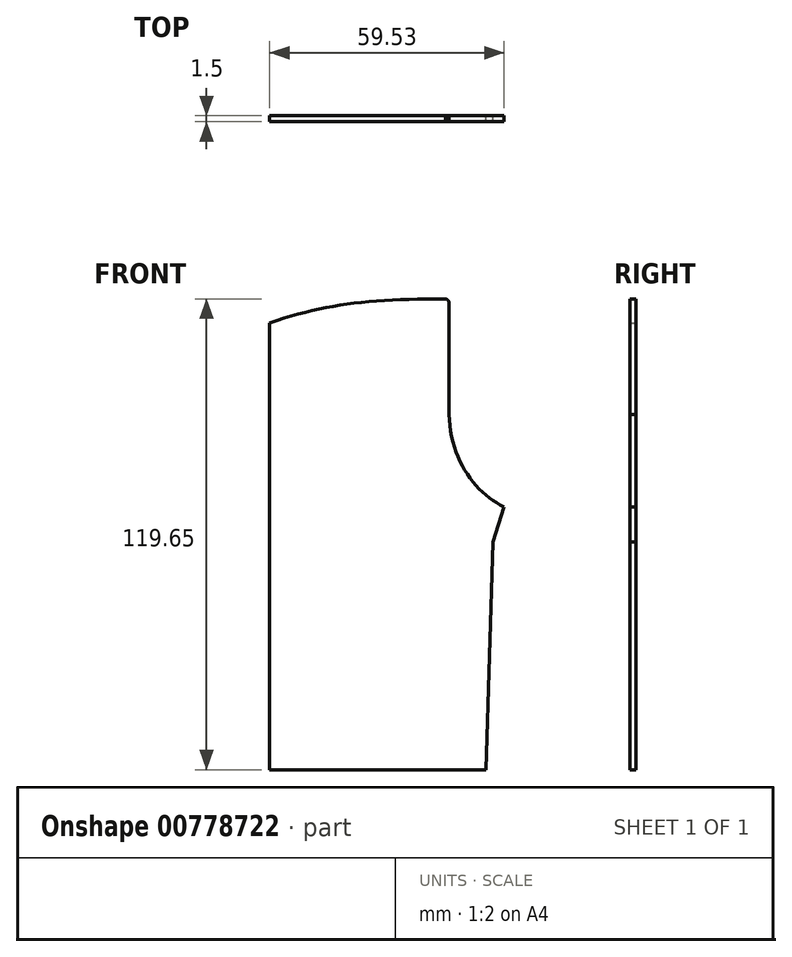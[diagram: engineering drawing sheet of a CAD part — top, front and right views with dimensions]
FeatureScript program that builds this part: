
annotation { "Feature Type Name" : "Feature", "Feature Type Description" : "" }
export const myFeature = defineFeature(function(context is Context, id is Id, definition is map)
    precondition{}
    {
        {
            var Q0;
            Q0=qCreatedBy(makeId("Front.planeOp"),FACE);
            var sketch = newSketch(context, id + "F0", { "sketchPlane" : qUnion([Q0])});
            skLineSegment(sketch, "E0", {"start": v(0, 0) * mm, "end": v(55, 0) * mm});
            skLineSegment(sketch, "E1", {"start": v(55, 0) * mm, "end": v(56.79, 57.84) * mm});
            skLineSegment(sketch, "E2", {"start": v(56.79, 57.84) * mm, "end": v(59.53, 66.82) * mm});
            skLineSegment(sketch, "E3", {"start": v(0, 0) * mm, "end": v(0, 113.54) * mm});
            skFitSpline(sketch, "E4", {"points": [v(0, 113.54) * mm, v(44.65, 119.65) * mm], "startDerivative": vector(42.5, 14.54) * mm, "endDerivative": vector(56.66, 0) * mm});
            skFitSpline(sketch, "E5", {"points": [v(44.65, 119.65) * mm, v(45.62, 118.32) * mm], "startDerivative": vector(1.89, -0.48) * mm, "endDerivative": vector(0, -2.29) * mm});
            skLineSegment(sketch, "E6", {"start": v(45.62, 118.32) * mm, "end": v(45.62, 90.3) * mm});
            skFitSpline(sketch, "E7", {"points": [v(45.62, 90.3) * mm, v(59.53, 66.82) * mm], "startDerivative": vector(0.44, -34.03) * mm, "endDerivative": vector(22, -10.48) * mm});
            skLineSegment(sketch, "E8", {"start": v(44.65, 119.65) * mm, "end": v(0, 119.65) * mm, "construction": true});
            skLineSegment(sketch, "E9", {"start": v(0, 119.65) * mm, "end": v(0, 113.54) * mm, "construction": true});
            skLineSegment(sketch, "E10", {"start": v(59.53, 66.82) * mm, "end": v(59.53, 0) * mm, "construction": true});
            skLineSegment(sketch, "E11", {"start": v(59.53, 0) * mm, "end": v(55, 0) * mm, "construction": true});
            skSolve(sketch);
        }
        {
            var Q0;
            Q0 = qSketchRegion(id + "F0", true);
            extrude(context, id + "F1", {"entities" : qUnion([Q0]), "depth" : 1.5 * mm, "offsetDistance" : 25 * mm});
        }
    });
